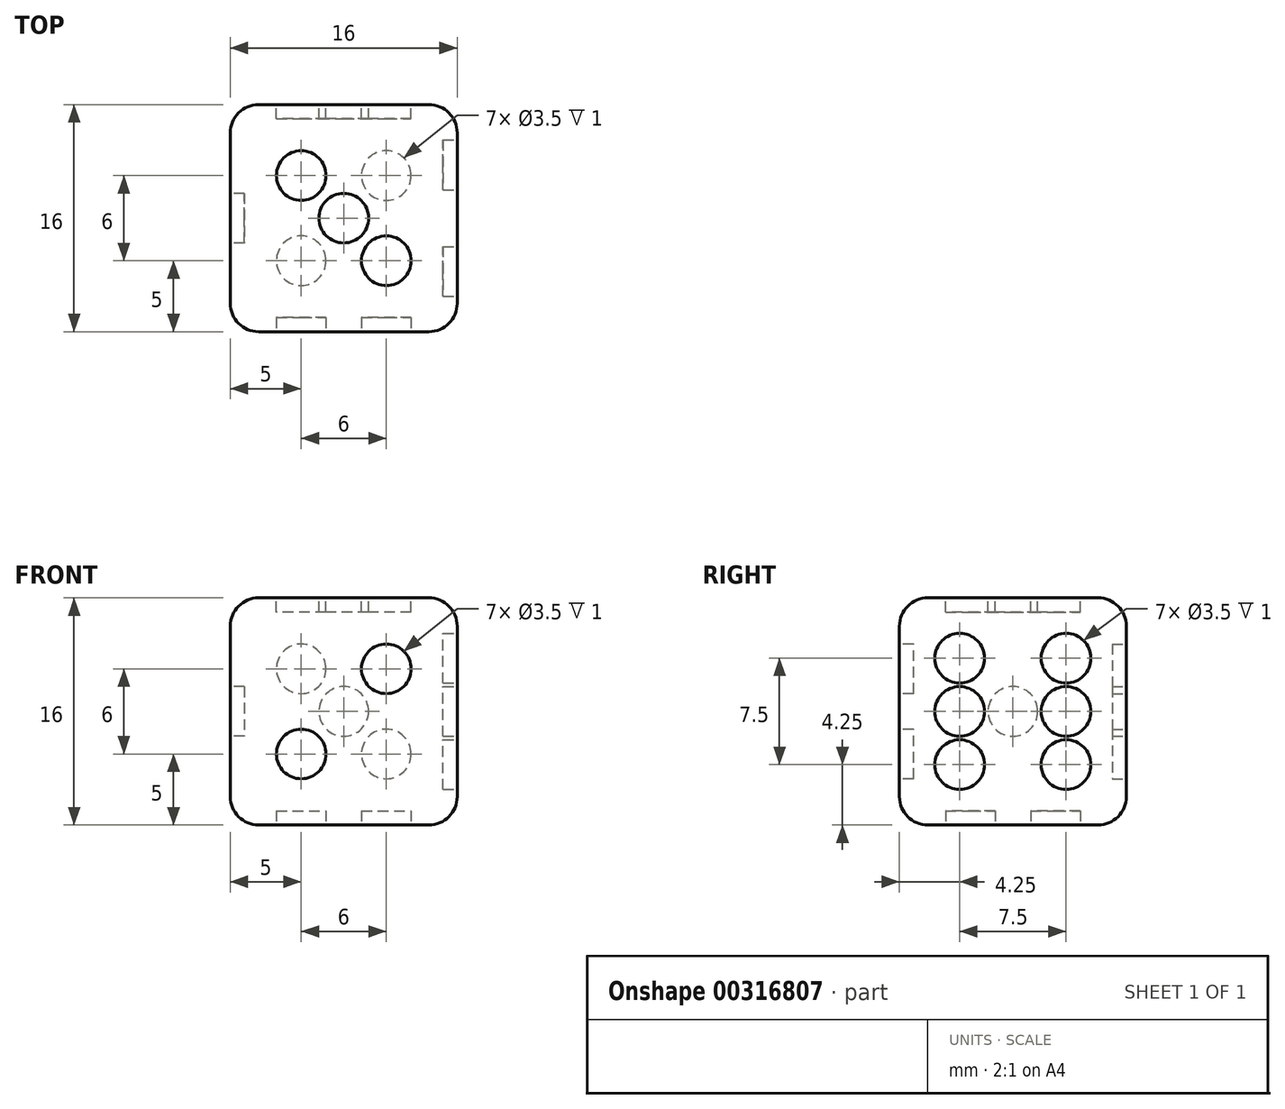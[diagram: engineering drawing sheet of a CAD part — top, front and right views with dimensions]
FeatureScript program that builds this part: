
annotation { "Feature Type Name" : "Feature", "Feature Type Description" : "" }
export const myFeature = defineFeature(function(context is Context, id is Id, definition is map)
    precondition{}
    {
        {
            var Q0;
            Q0=qCreatedBy(makeId("Front.planeOp"),FACE);
            var sketch = newSketch(context, id + "F0", { "sketchPlane" : qUnion([Q0])});
            skLineSegment(sketch, "E0.bottom", {"start": v(8, 8) * mm, "end": v(-8, 8) * mm});
            skLineSegment(sketch, "E0.top", {"start": v(8, -8) * mm, "end": v(-8, -8) * mm});
            skLineSegment(sketch, "E0.left", {"start": v(8, 8) * mm, "end": v(8, -8) * mm});
            skLineSegment(sketch, "E0.right", {"start": v(-8, 8) * mm, "end": v(-8, -8) * mm});
            skPoint(sketch, "E0.middle", {"position": v(0, 0) * mm});
            skSolve(sketch);
        }
        {
            var Q0;
            Q0 = qSketchRegion(id + "F0", true);
            extrude(context, id + "F1", {"entities" : qUnion([Q0]), "depth" : 16 * mm});
        }
        {
            var Q0;
            Q0=makeQuery(id+"F1.opExtrude","CAP_EDGE",EDGE,{"disambiguationData":[OSD([sQuery(id+"F0.wireOp",EDGE,"E0.bottom")])],"isStart":false});
            var Q1;
            Q1=makeQuery(id+"F1.opExtrude","SWEPT_EDGE",EDGE,{"disambiguationData":[OSD([sQuery(id+"F0.wireOp",EDGE,"E0.bottom"),sQuery(id+"F0.wireOp",EDGE,"E0.right")])]});
            var Q2;
            Q2=makeQuery(id+"F1.opExtrude","SWEPT_EDGE",EDGE,{"disambiguationData":[OSD([sQuery(id+"F0.wireOp",EDGE,"E0.bottom"),sQuery(id+"F0.wireOp",EDGE,"E0.left")])]});
            var Q3;
            Q3=makeQuery(id+"F1.opExtrude","CAP_EDGE",EDGE,{"disambiguationData":[OSD([sQuery(id+"F0.wireOp",EDGE,"E0.bottom")])],"isStart":true});
            var Q4;
            Q4=makeQuery(id+"F1.opExtrude","CAP_EDGE",EDGE,{"disambiguationData":[OSD([sQuery(id+"F0.wireOp",EDGE,"E0.top")])],"isStart":true});
            var Q5;
            Q5=makeQuery(id+"F1.opExtrude","CAP_EDGE",EDGE,{"disambiguationData":[OSD([sQuery(id+"F0.wireOp",EDGE,"E0.left")])],"isStart":true});
            var Q6;
            Q6=makeQuery(id+"F1.opExtrude","SWEPT_EDGE",EDGE,{"disambiguationData":[OSD([sQuery(id+"F0.wireOp",EDGE,"E0.top"),sQuery(id+"F0.wireOp",EDGE,"E0.right")])]});
            var Q7;
            Q7=makeQuery(id+"F1.opExtrude","CAP_EDGE",EDGE,{"disambiguationData":[OSD([sQuery(id+"F0.wireOp",EDGE,"E0.right")])],"isStart":false});
            var Q8;
            Q8=makeQuery(id+"F1.opExtrude","CAP_EDGE",EDGE,{"disambiguationData":[OSD([sQuery(id+"F0.wireOp",EDGE,"E0.right")])],"isStart":true});
            var Q9;
            Q9=makeQuery(id+"F1.opExtrude","CAP_EDGE",EDGE,{"disambiguationData":[OSD([sQuery(id+"F0.wireOp",EDGE,"E0.top")])],"isStart":false});
            var Q10;
            Q10=makeQuery(id+"F1.opExtrude","CAP_EDGE",EDGE,{"disambiguationData":[OSD([sQuery(id+"F0.wireOp",EDGE,"E0.left")])],"isStart":false});
            var Q11;
            Q11=makeQuery(id+"F1.opExtrude","SWEPT_EDGE",EDGE,{"disambiguationData":[OSD([sQuery(id+"F0.wireOp",EDGE,"E0.top"),sQuery(id+"F0.wireOp",EDGE,"E0.left")])]});
            fillet(context, id + "F2", {"entities" : qUnion([Q0, Q1, Q2, Q3, Q4, Q5, Q6, Q7, Q8, Q9, Q10, Q11]), "radius" : 2 * mm, "tangentPropagation" : true, "allowEdgeOverflow" : false});
        }
        {
            var Q0;
            Q0=makeQuery(id+"F1.opExtrude","CAP_FACE",FACE,{"disambiguationData":[OSD([sQuery(id+"F0.wireOp",EDGE,"E0.bottom"),sQuery(id+"F0.wireOp",EDGE,"E0.top"),sQuery(id+"F0.wireOp",EDGE,"E0.left"),sQuery(id+"F0.wireOp",EDGE,"E0.right")])],"isStart":false});
            var sketch = newSketch(context, id + "F3", { "sketchPlane" : qUnion([Q0])});
            skLineSegment(sketch, "E1.bottom", {"start": v(3, 3) * mm, "end": v(-3, 3) * mm});
            skLineSegment(sketch, "E1.top", {"start": v(3, -3) * mm, "end": v(-3, -3) * mm});
            skLineSegment(sketch, "E1.left", {"start": v(3, 3) * mm, "end": v(3, -3) * mm});
            skLineSegment(sketch, "E1.right", {"start": v(-3, 3) * mm, "end": v(-3, -3) * mm});
            skPoint(sketch, "E1.middle", {"position": v(0, 0) * mm});
            skCircle(sketch, "E2", {"center": v(-3, -3) * mm, "radius": 1.75 * mm});
            skCircle(sketch, "E3", {"center": v(3, 3) * mm, "radius": 1.75 * mm});
            skSolve(sketch);
        }
        {
            var Q0;
            {var subQ0=sQuery(id+"F3.wireOp",EDGE,"E1.left");var subQ1=sQuery(id+"F3.wireOp",EDGE,"E1.bottom");var subQ2=makeQuery(id+"F3.imprint","INTERSECT",VERTEX,{"derivedFrom":[subQ1,subQ0]});Q0=makeQuery(id+"F3.imprint","IMPRINT",FACE,{"disambiguationData":[TD([[makeQuery(id+"F3.imprint","IMPRINT",EDGE,{"disambiguationData":[TD([[subQ2,-1.0]])],"derivedFrom":subQ1}),1.0]])]});}
            var Q1;
            {var subQ0=sQuery(id+"F3.wireOp",EDGE,"E1.right");var subQ1=sQuery(id+"F3.wireOp",EDGE,"E1.top");var subQ2=makeQuery(id+"F3.imprint","INTERSECT",VERTEX,{"derivedFrom":[subQ1,subQ0]});Q1=makeQuery(id+"F3.imprint","IMPRINT",FACE,{"disambiguationData":[TD([[makeQuery(id+"F3.imprint","IMPRINT",EDGE,{"disambiguationData":[TD([[subQ2,1.0]])],"derivedFrom":subQ1}),1.0]])]});}
            var Q2;
            {var subQ0=sQuery(id+"F3.wireOp",EDGE,"E1.right");var subQ1=sQuery(id+"F3.wireOp",EDGE,"E1.top");var subQ2=makeQuery(id+"F3.imprint","INTERSECT",VERTEX,{"derivedFrom":[subQ1,subQ0]});Q2=makeQuery(id+"F3.imprint","IMPRINT",FACE,{"disambiguationData":[TD([[makeQuery(id+"F3.imprint","IMPRINT",EDGE,{"disambiguationData":[TD([[subQ2,1.0]])],"derivedFrom":subQ1}),-1.0]])]});}
            var Q3;
            {var subQ0=sQuery(id+"F3.wireOp",EDGE,"E1.left");var subQ1=sQuery(id+"F3.wireOp",EDGE,"E1.bottom");var subQ2=makeQuery(id+"F3.imprint","INTERSECT",VERTEX,{"derivedFrom":[subQ1,subQ0]});Q3=makeQuery(id+"F3.imprint","IMPRINT",FACE,{"disambiguationData":[TD([[makeQuery(id+"F3.imprint","IMPRINT",EDGE,{"disambiguationData":[TD([[subQ2,-1.0]])],"derivedFrom":subQ1}),-1.0]])]});}
            extrude(context, id + "F4", {"entities" : qUnion([Q0, Q1, Q2, Q3]), "operationType" : NewBodyOperationType.REMOVE, "oppositeDirection" : true, "depth" : 1 * mm});
        }
        {
            var Q0;
            Q0=makeQuery(id+"F1.opExtrude","SWEPT_FACE",FACE,{"disambiguationData":[OSD([sQuery(id+"F0.wireOp",EDGE,"E0.bottom")])]});
            var sketch = newSketch(context, id + "F5", { "sketchPlane" : qUnion([Q0])});
            skLineSegment(sketch, "E4.bottom", {"start": v(3, -5) * mm, "end": v(-3, -5) * mm});
            skLineSegment(sketch, "E4.top", {"start": v(3, -11) * mm, "end": v(-3, -11) * mm});
            skLineSegment(sketch, "E4.left", {"start": v(3, -5) * mm, "end": v(3, -11) * mm});
            skLineSegment(sketch, "E4.right", {"start": v(-3, -5) * mm, "end": v(-3, -11) * mm});
            skPoint(sketch, "E4.middle", {"position": v(0, -8) * mm});
            skPoint(sketch, "E4.middle.positionSnap0", {"position": v(6, -8) * mm});
            skPoint(sketch, "E4.middle.positionSnap1", {"position": v(0, -14) * mm});
            skPoint(sketch, "E4.centerSnap0", {"position": v(6, -8) * mm});
            skPoint(sketch, "E4.centerSnap1", {"position": v(0, -14) * mm});
            skCircle(sketch, "E5", {"center": v(3, -11) * mm, "radius": 1.75 * mm});
            skCircle(sketch, "E6", {"center": v(0, -8) * mm, "radius": 1.75 * mm});
            skCircle(sketch, "E7", {"center": v(-3, -5) * mm, "radius": 1.75 * mm});
            skSolve(sketch);
        }
        {
            var Q0;
            {var subQ0=sQuery(id+"F5.wireOp",EDGE,"E4.right");var subQ1=sQuery(id+"F5.wireOp",EDGE,"E4.bottom");var subQ2=makeQuery(id+"F5.imprint","INTERSECT",VERTEX,{"derivedFrom":[subQ1,subQ0]});Q0=makeQuery(id+"F5.imprint","IMPRINT",FACE,{"disambiguationData":[TD([[makeQuery(id+"F5.imprint","IMPRINT",EDGE,{"disambiguationData":[TD([[subQ2,1.0]])],"derivedFrom":subQ1}),-1.0]])]});}
            var Q1;
            {var subQ0=sQuery(id+"F5.wireOp",EDGE,"E4.right");var subQ1=sQuery(id+"F5.wireOp",EDGE,"E4.bottom");var subQ2=makeQuery(id+"F5.imprint","INTERSECT",VERTEX,{"derivedFrom":[subQ1,subQ0]});Q1=makeQuery(id+"F5.imprint","IMPRINT",FACE,{"disambiguationData":[TD([[makeQuery(id+"F5.imprint","IMPRINT",EDGE,{"disambiguationData":[TD([[subQ2,1.0]])],"derivedFrom":subQ1}),1.0]])]});}
            var Q2;
            {var subQ0=sQuery(id+"F5.wireOp",EDGE,"E4.left");var subQ1=sQuery(id+"F5.wireOp",EDGE,"E4.top");var subQ2=makeQuery(id+"F5.imprint","INTERSECT",VERTEX,{"derivedFrom":[subQ1,subQ0]});Q2=makeQuery(id+"F5.imprint","IMPRINT",FACE,{"disambiguationData":[TD([[makeQuery(id+"F5.imprint","IMPRINT",EDGE,{"disambiguationData":[TD([[subQ2,-1.0]])],"derivedFrom":subQ1}),-1.0]])]});}
            var Q3;
            {var subQ0=sQuery(id+"F5.wireOp",EDGE,"E4.left");var subQ1=sQuery(id+"F5.wireOp",EDGE,"E4.top");var subQ2=makeQuery(id+"F5.imprint","INTERSECT",VERTEX,{"derivedFrom":[subQ1,subQ0]});Q3=makeQuery(id+"F5.imprint","IMPRINT",FACE,{"disambiguationData":[TD([[makeQuery(id+"F5.imprint","IMPRINT",EDGE,{"disambiguationData":[TD([[subQ2,-1.0]])],"derivedFrom":subQ1}),1.0]])]});}
            var Q4;
            Q4=makeQuery(id+"F5.imprint","IMPRINT",FACE,{"disambiguationData":[TD([[makeQuery(id+"F5.imprint","IMPRINT",EDGE,{"derivedFrom":sQuery(id+"F5.wireOp",EDGE,"E6")}),1.0]])]});
            extrude(context, id + "F6", {"entities" : qUnion([Q0, Q1, Q2, Q3, Q4]), "operationType" : NewBodyOperationType.REMOVE, "oppositeDirection" : true, "depth" : 1 * mm});
        }
        {
            var Q0;
            Q0=makeQuery(id+"F1.opExtrude","SWEPT_FACE",FACE,{"disambiguationData":[OSD([sQuery(id+"F0.wireOp",EDGE,"E0.left")])]});
            var sketch = newSketch(context, id + "F7", { "sketchPlane" : qUnion([Q0])});
            skLineSegment(sketch, "E8.bottom", {"start": v(-4.25, 3.75) * mm, "end": v(-11.75, 3.75) * mm});
            skLineSegment(sketch, "E8.top", {"start": v(-4.25, -3.75) * mm, "end": v(-11.75, -3.75) * mm});
            skLineSegment(sketch, "E8.left", {"start": v(-4.25, 3.75) * mm, "end": v(-4.25, -3.75) * mm});
            skLineSegment(sketch, "E8.right", {"start": v(-11.75, 3.75) * mm, "end": v(-11.75, -3.75) * mm});
            skPoint(sketch, "E8.middle", {"position": v(-8, 0) * mm});
            skPoint(sketch, "E8.middle.positionSnap0", {"position": v(-8, -6) * mm});
            skPoint(sketch, "E8.middle.positionSnap1", {"position": v(-14, 0) * mm});
            skPoint(sketch, "E8.centerSnap0", {"position": v(-8, -6) * mm});
            skPoint(sketch, "E8.centerSnap1", {"position": v(-14, 0) * mm});
            skCircle(sketch, "E9", {"center": v(-11.75, 3.75) * mm, "radius": 1.75 * mm});
            skCircle(sketch, "E10", {"center": v(-4.25, 3.75) * mm, "radius": 1.75 * mm});
            skCircle(sketch, "E11", {"center": v(-4.25, 0) * mm, "radius": 1.75 * mm});
            skCircle(sketch, "E12", {"center": v(-4.25, -3.75) * mm, "radius": 1.75 * mm});
            skCircle(sketch, "E13", {"center": v(-11.75, -3.75) * mm, "radius": 1.75 * mm});
            skCircle(sketch, "E14", {"center": v(-11.75, 0) * mm, "radius": 1.75 * mm});
            skSolve(sketch);
        }
        {
            var Q0;
            {var subQ0=sQuery(id+"F7.wireOp",EDGE,"E8.left");var subQ1=sQuery(id+"F7.wireOp",EDGE,"E8.bottom");var subQ2=makeQuery(id+"F7.imprint","INTERSECT",VERTEX,{"derivedFrom":[subQ1,subQ0]});Q0=makeQuery(id+"F7.imprint","IMPRINT",FACE,{"disambiguationData":[TD([[makeQuery(id+"F7.imprint","IMPRINT",EDGE,{"disambiguationData":[TD([[subQ2,-1.0]])],"derivedFrom":subQ1}),1.0]])]});}
            var Q1;
            {var subQ0=sQuery(id+"F7.wireOp",EDGE,"E8.left");var subQ1=sQuery(id+"F7.wireOp",EDGE,"E8.bottom");var subQ2=makeQuery(id+"F7.imprint","INTERSECT",VERTEX,{"derivedFrom":[subQ1,subQ0]});Q1=makeQuery(id+"F7.imprint","IMPRINT",FACE,{"disambiguationData":[TD([[makeQuery(id+"F7.imprint","IMPRINT",EDGE,{"disambiguationData":[TD([[subQ2,-1.0]])],"derivedFrom":subQ1}),-1.0]])]});}
            var Q2;
            {var subQ0=sQuery(id+"F7.wireOp",EDGE,"E8.right");var subQ1=sQuery(id+"F7.wireOp",EDGE,"E8.bottom");var subQ2=makeQuery(id+"F7.imprint","INTERSECT",VERTEX,{"derivedFrom":[subQ1,subQ0]});Q2=makeQuery(id+"F7.imprint","IMPRINT",FACE,{"disambiguationData":[TD([[makeQuery(id+"F7.imprint","IMPRINT",EDGE,{"disambiguationData":[TD([[subQ2,1.0]])],"derivedFrom":subQ1}),-1.0]])]});}
            var Q3;
            {var subQ0=sQuery(id+"F7.wireOp",EDGE,"E8.right");var subQ1=sQuery(id+"F7.wireOp",EDGE,"E8.bottom");var subQ2=makeQuery(id+"F7.imprint","INTERSECT",VERTEX,{"derivedFrom":[subQ1,subQ0]});Q3=makeQuery(id+"F7.imprint","IMPRINT",FACE,{"disambiguationData":[TD([[makeQuery(id+"F7.imprint","IMPRINT",EDGE,{"disambiguationData":[TD([[subQ2,1.0]])],"derivedFrom":subQ1}),1.0]])]});}
            var Q4;
            {var subQ0=sQuery(id+"F7.wireOp",EDGE,"E8.left");var subQ1=sQuery(id+"F7.wireOp",EDGE,"E8.top");var subQ2=makeQuery(id+"F7.imprint","INTERSECT",VERTEX,{"derivedFrom":[subQ1,subQ0]});Q4=makeQuery(id+"F7.imprint","IMPRINT",FACE,{"disambiguationData":[TD([[makeQuery(id+"F7.imprint","IMPRINT",EDGE,{"disambiguationData":[TD([[subQ2,-1.0]])],"derivedFrom":subQ1}),-1.0]])]});}
            var Q5;
            {var subQ0=sQuery(id+"F7.wireOp",EDGE,"E8.left");var subQ1=sQuery(id+"F7.wireOp",EDGE,"E8.top");var subQ2=makeQuery(id+"F7.imprint","INTERSECT",VERTEX,{"derivedFrom":[subQ1,subQ0]});Q5=makeQuery(id+"F7.imprint","IMPRINT",FACE,{"disambiguationData":[TD([[makeQuery(id+"F7.imprint","IMPRINT",EDGE,{"disambiguationData":[TD([[subQ2,-1.0]])],"derivedFrom":subQ1}),1.0]])]});}
            var Q6;
            {var subQ0=sQuery(id+"F7.wireOp",EDGE,"E8.right");var subQ1=sQuery(id+"F7.wireOp",EDGE,"E8.top");var subQ2=makeQuery(id+"F7.imprint","INTERSECT",VERTEX,{"derivedFrom":[subQ1,subQ0]});Q6=makeQuery(id+"F7.imprint","IMPRINT",FACE,{"disambiguationData":[TD([[makeQuery(id+"F7.imprint","IMPRINT",EDGE,{"disambiguationData":[TD([[subQ2,1.0]])],"derivedFrom":subQ1}),-1.0]])]});}
            var Q7;
            {var subQ0=sQuery(id+"F7.wireOp",EDGE,"E8.right");var subQ1=sQuery(id+"F7.wireOp",EDGE,"E8.top");var subQ2=makeQuery(id+"F7.imprint","INTERSECT",VERTEX,{"derivedFrom":[subQ1,subQ0]});Q7=makeQuery(id+"F7.imprint","IMPRINT",FACE,{"disambiguationData":[TD([[makeQuery(id+"F7.imprint","IMPRINT",EDGE,{"disambiguationData":[TD([[subQ2,1.0]])],"derivedFrom":subQ1}),1.0]])]});}
            var Q8;
            {var subQ0=sQuery(id+"F7.wireOp",EDGE,"E11");var subQ1=sQuery(id+"F7.wireOp",EDGE,"E8.left");var subQ2=makeQuery(id+"F7.imprint","INTERSECT",VERTEX,{"disambiguationData":[OD(0.0)],"derivedFrom":[subQ1,subQ0]});Q8=makeQuery(id+"F7.imprint","IMPRINT",FACE,{"disambiguationData":[TD([[makeQuery(id+"F7.imprint","IMPRINT",EDGE,{"disambiguationData":[TD([[subQ2,-1.0]])],"derivedFrom":subQ1}),-1.0]])]});}
            var Q9;
            {var subQ0=sQuery(id+"F7.wireOp",EDGE,"E11");var subQ1=sQuery(id+"F7.wireOp",EDGE,"E8.left");var subQ2=makeQuery(id+"F7.imprint","INTERSECT",VERTEX,{"disambiguationData":[OD(0.0)],"derivedFrom":[subQ1,subQ0]});Q9=makeQuery(id+"F7.imprint","IMPRINT",FACE,{"disambiguationData":[TD([[makeQuery(id+"F7.imprint","IMPRINT",EDGE,{"disambiguationData":[TD([[subQ2,-1.0]])],"derivedFrom":subQ1}),1.0]])]});}
            var Q10;
            {var subQ0=sQuery(id+"F7.wireOp",EDGE,"E14");var subQ1=sQuery(id+"F7.wireOp",EDGE,"E8.right");var subQ2=makeQuery(id+"F7.imprint","INTERSECT",VERTEX,{"disambiguationData":[OD(0.0)],"derivedFrom":[subQ1,subQ0]});Q10=makeQuery(id+"F7.imprint","IMPRINT",FACE,{"disambiguationData":[TD([[makeQuery(id+"F7.imprint","IMPRINT",EDGE,{"disambiguationData":[TD([[subQ2,-1.0]])],"derivedFrom":subQ1}),-1.0]])]});}
            var Q11;
            {var subQ0=sQuery(id+"F7.wireOp",EDGE,"E14");var subQ1=sQuery(id+"F7.wireOp",EDGE,"E8.right");var subQ2=makeQuery(id+"F7.imprint","INTERSECT",VERTEX,{"disambiguationData":[OD(0.0)],"derivedFrom":[subQ1,subQ0]});Q11=makeQuery(id+"F7.imprint","IMPRINT",FACE,{"disambiguationData":[TD([[makeQuery(id+"F7.imprint","IMPRINT",EDGE,{"disambiguationData":[TD([[subQ2,-1.0]])],"derivedFrom":subQ1}),1.0]])]});}
            extrude(context, id + "F8", {"entities" : qUnion([Q0, Q1, Q2, Q3, Q4, Q5, Q6, Q7, Q8, Q9, Q10, Q11]), "operationType" : NewBodyOperationType.REMOVE, "oppositeDirection" : true, "depth" : 1 * mm});
        }
        {
            var Q0;
            Q0=makeQuery(id+"F1.opExtrude","SWEPT_FACE",FACE,{"disambiguationData":[OSD([sQuery(id+"F0.wireOp",EDGE,"E0.top")])]});
            var sketch = newSketch(context, id + "F9", { "sketchPlane" : qUnion([Q0])});
            skLineSegment(sketch, "E15.bottom", {"start": v(3, 11) * mm, "end": v(-3, 11) * mm});
            skLineSegment(sketch, "E15.top", {"start": v(3, 5) * mm, "end": v(-3, 5) * mm});
            skLineSegment(sketch, "E15.left", {"start": v(3, 11) * mm, "end": v(3, 5) * mm});
            skLineSegment(sketch, "E15.right", {"start": v(-3, 11) * mm, "end": v(-3, 5) * mm});
            skPoint(sketch, "E15.middle", {"position": v(0, 8) * mm});
            skPoint(sketch, "E15.middle.positionSnap0", {"position": v(6, 8) * mm});
            skPoint(sketch, "E15.centerSnap0", {"position": v(6, 8) * mm});
            skCircle(sketch, "E16", {"center": v(-3, 11) * mm, "radius": 1.75 * mm});
            skCircle(sketch, "E17", {"center": v(3, 11) * mm, "radius": 1.75 * mm});
            skCircle(sketch, "E18", {"center": v(3, 5) * mm, "radius": 1.75 * mm});
            skCircle(sketch, "E19", {"center": v(-3, 5) * mm, "radius": 1.75 * mm});
            skSolve(sketch);
        }
        {
            var Q0;
            {var subQ0=sQuery(id+"F9.wireOp",EDGE,"E15.left");var subQ1=sQuery(id+"F9.wireOp",EDGE,"E15.bottom");var subQ2=makeQuery(id+"F9.imprint","INTERSECT",VERTEX,{"derivedFrom":[subQ1,subQ0]});Q0=makeQuery(id+"F9.imprint","IMPRINT",FACE,{"disambiguationData":[TD([[makeQuery(id+"F9.imprint","IMPRINT",EDGE,{"disambiguationData":[TD([[subQ2,-1.0]])],"derivedFrom":subQ1}),1.0]])]});}
            var Q1;
            {var subQ0=sQuery(id+"F9.wireOp",EDGE,"E15.left");var subQ1=sQuery(id+"F9.wireOp",EDGE,"E15.bottom");var subQ2=makeQuery(id+"F9.imprint","INTERSECT",VERTEX,{"derivedFrom":[subQ1,subQ0]});Q1=makeQuery(id+"F9.imprint","IMPRINT",FACE,{"disambiguationData":[TD([[makeQuery(id+"F9.imprint","IMPRINT",EDGE,{"disambiguationData":[TD([[subQ2,-1.0]])],"derivedFrom":subQ1}),-1.0]])]});}
            var Q2;
            {var subQ0=sQuery(id+"F9.wireOp",EDGE,"E15.right");var subQ1=sQuery(id+"F9.wireOp",EDGE,"E15.bottom");var subQ2=makeQuery(id+"F9.imprint","INTERSECT",VERTEX,{"derivedFrom":[subQ1,subQ0]});Q2=makeQuery(id+"F9.imprint","IMPRINT",FACE,{"disambiguationData":[TD([[makeQuery(id+"F9.imprint","IMPRINT",EDGE,{"disambiguationData":[TD([[subQ2,1.0]])],"derivedFrom":subQ1}),-1.0]])]});}
            var Q3;
            {var subQ0=sQuery(id+"F9.wireOp",EDGE,"E15.right");var subQ1=sQuery(id+"F9.wireOp",EDGE,"E15.bottom");var subQ2=makeQuery(id+"F9.imprint","INTERSECT",VERTEX,{"derivedFrom":[subQ1,subQ0]});Q3=makeQuery(id+"F9.imprint","IMPRINT",FACE,{"disambiguationData":[TD([[makeQuery(id+"F9.imprint","IMPRINT",EDGE,{"disambiguationData":[TD([[subQ2,1.0]])],"derivedFrom":subQ1}),1.0]])]});}
            var Q4;
            {var subQ0=sQuery(id+"F9.wireOp",EDGE,"E15.left");var subQ1=sQuery(id+"F9.wireOp",EDGE,"E15.top");var subQ2=makeQuery(id+"F9.imprint","INTERSECT",VERTEX,{"derivedFrom":[subQ1,subQ0]});Q4=makeQuery(id+"F9.imprint","IMPRINT",FACE,{"disambiguationData":[TD([[makeQuery(id+"F9.imprint","IMPRINT",EDGE,{"disambiguationData":[TD([[subQ2,-1.0]])],"derivedFrom":subQ1}),-1.0]])]});}
            var Q5;
            {var subQ0=sQuery(id+"F9.wireOp",EDGE,"E15.left");var subQ1=sQuery(id+"F9.wireOp",EDGE,"E15.top");var subQ2=makeQuery(id+"F9.imprint","INTERSECT",VERTEX,{"derivedFrom":[subQ1,subQ0]});Q5=makeQuery(id+"F9.imprint","IMPRINT",FACE,{"disambiguationData":[TD([[makeQuery(id+"F9.imprint","IMPRINT",EDGE,{"disambiguationData":[TD([[subQ2,-1.0]])],"derivedFrom":subQ1}),1.0]])]});}
            var Q6;
            {var subQ0=sQuery(id+"F9.wireOp",EDGE,"E15.right");var subQ1=sQuery(id+"F9.wireOp",EDGE,"E15.top");var subQ2=makeQuery(id+"F9.imprint","INTERSECT",VERTEX,{"derivedFrom":[subQ1,subQ0]});Q6=makeQuery(id+"F9.imprint","IMPRINT",FACE,{"disambiguationData":[TD([[makeQuery(id+"F9.imprint","IMPRINT",EDGE,{"disambiguationData":[TD([[subQ2,1.0]])],"derivedFrom":subQ1}),-1.0]])]});}
            var Q7;
            {var subQ0=sQuery(id+"F9.wireOp",EDGE,"E15.right");var subQ1=sQuery(id+"F9.wireOp",EDGE,"E15.top");var subQ2=makeQuery(id+"F9.imprint","INTERSECT",VERTEX,{"derivedFrom":[subQ1,subQ0]});Q7=makeQuery(id+"F9.imprint","IMPRINT",FACE,{"disambiguationData":[TD([[makeQuery(id+"F9.imprint","IMPRINT",EDGE,{"disambiguationData":[TD([[subQ2,1.0]])],"derivedFrom":subQ1}),1.0]])]});}
            extrude(context, id + "F10", {"entities" : qUnion([Q0, Q1, Q2, Q3, Q4, Q5, Q6, Q7]), "operationType" : NewBodyOperationType.REMOVE, "oppositeDirection" : true, "depth" : 1 * mm});
        }
        {
            var Q0;
            Q0=makeQuery(id+"F1.opExtrude","SWEPT_FACE",FACE,{"disambiguationData":[OSD([sQuery(id+"F0.wireOp",EDGE,"E0.right")])]});
            var sketch = newSketch(context, id + "F11", { "sketchPlane" : qUnion([Q0])});
            skCircle(sketch, "E20", {"center": v(8, 0) * mm, "radius": 1.75 * mm});
            skPoint(sketch, "E20.centerSnap0", {"position": v(8, -6) * mm});
            skSolve(sketch);
        }
        {
            var Q0;
            Q0 = qSketchRegion(id + "F11", true);
            extrude(context, id + "F12", {"entities" : qUnion([Q0]), "operationType" : NewBodyOperationType.REMOVE, "oppositeDirection" : true, "depth" : 1 * mm});
        }
        {
            var Q0;
            Q0=makeQuery(id+"F1.opExtrude","CAP_FACE",FACE,{"disambiguationData":[OSD([sQuery(id+"F0.wireOp",EDGE,"E0.bottom"),sQuery(id+"F0.wireOp",EDGE,"E0.top"),sQuery(id+"F0.wireOp",EDGE,"E0.left"),sQuery(id+"F0.wireOp",EDGE,"E0.right")])],"isStart":true});
            var sketch = newSketch(context, id + "F13", { "sketchPlane" : qUnion([Q0])});
            skLineSegment(sketch, "E21.bottom", {"start": v(3, 3) * mm, "end": v(-3, 3) * mm});
            skLineSegment(sketch, "E21.top", {"start": v(3, -3) * mm, "end": v(-3, -3) * mm});
            skLineSegment(sketch, "E21.left", {"start": v(3, 3) * mm, "end": v(3, -3) * mm});
            skLineSegment(sketch, "E21.right", {"start": v(-3, 3) * mm, "end": v(-3, -3) * mm});
            skPoint(sketch, "E21.middle", {"position": v(0, 0) * mm});
            skCircle(sketch, "E22", {"center": v(-3, 3) * mm, "radius": 1.75 * mm});
            skCircle(sketch, "E23", {"center": v(-3, -3) * mm, "radius": 1.75 * mm});
            skCircle(sketch, "E24", {"center": v(0, 0) * mm, "radius": 1.75 * mm});
            skCircle(sketch, "E25", {"center": v(3, 3) * mm, "radius": 1.75 * mm});
            skCircle(sketch, "E26", {"center": v(3, -3) * mm, "radius": 1.75 * mm});
            skSolve(sketch);
        }
        {
            var Q0;
            {var subQ0=sQuery(id+"F13.wireOp",EDGE,"E21.left");var subQ1=sQuery(id+"F13.wireOp",EDGE,"E21.bottom");var subQ2=makeQuery(id+"F13.imprint","INTERSECT",VERTEX,{"derivedFrom":[subQ1,subQ0]});Q0=makeQuery(id+"F13.imprint","IMPRINT",FACE,{"disambiguationData":[TD([[makeQuery(id+"F13.imprint","IMPRINT",EDGE,{"disambiguationData":[TD([[subQ2,-1.0]])],"derivedFrom":subQ1}),1.0]])]});}
            var Q1;
            {var subQ0=sQuery(id+"F13.wireOp",EDGE,"E21.left");var subQ1=sQuery(id+"F13.wireOp",EDGE,"E21.bottom");var subQ2=makeQuery(id+"F13.imprint","INTERSECT",VERTEX,{"derivedFrom":[subQ1,subQ0]});Q1=makeQuery(id+"F13.imprint","IMPRINT",FACE,{"disambiguationData":[TD([[makeQuery(id+"F13.imprint","IMPRINT",EDGE,{"disambiguationData":[TD([[subQ2,-1.0]])],"derivedFrom":subQ1}),-1.0]])]});}
            var Q2;
            {var subQ0=sQuery(id+"F13.wireOp",EDGE,"E21.right");var subQ1=sQuery(id+"F13.wireOp",EDGE,"E21.bottom");var subQ2=makeQuery(id+"F13.imprint","INTERSECT",VERTEX,{"derivedFrom":[subQ1,subQ0]});Q2=makeQuery(id+"F13.imprint","IMPRINT",FACE,{"disambiguationData":[TD([[makeQuery(id+"F13.imprint","IMPRINT",EDGE,{"disambiguationData":[TD([[subQ2,1.0]])],"derivedFrom":subQ1}),-1.0]])]});}
            var Q3;
            {var subQ0=sQuery(id+"F13.wireOp",EDGE,"E21.right");var subQ1=sQuery(id+"F13.wireOp",EDGE,"E21.bottom");var subQ2=makeQuery(id+"F13.imprint","INTERSECT",VERTEX,{"derivedFrom":[subQ1,subQ0]});Q3=makeQuery(id+"F13.imprint","IMPRINT",FACE,{"disambiguationData":[TD([[makeQuery(id+"F13.imprint","IMPRINT",EDGE,{"disambiguationData":[TD([[subQ2,1.0]])],"derivedFrom":subQ1}),1.0]])]});}
            var Q4;
            {var subQ0=sQuery(id+"F13.wireOp",EDGE,"E21.left");var subQ1=sQuery(id+"F13.wireOp",EDGE,"E21.top");var subQ2=makeQuery(id+"F13.imprint","INTERSECT",VERTEX,{"derivedFrom":[subQ1,subQ0]});Q4=makeQuery(id+"F13.imprint","IMPRINT",FACE,{"disambiguationData":[TD([[makeQuery(id+"F13.imprint","IMPRINT",EDGE,{"disambiguationData":[TD([[subQ2,-1.0]])],"derivedFrom":subQ1}),-1.0]])]});}
            var Q5;
            {var subQ0=sQuery(id+"F13.wireOp",EDGE,"E21.left");var subQ1=sQuery(id+"F13.wireOp",EDGE,"E21.top");var subQ2=makeQuery(id+"F13.imprint","INTERSECT",VERTEX,{"derivedFrom":[subQ1,subQ0]});Q5=makeQuery(id+"F13.imprint","IMPRINT",FACE,{"disambiguationData":[TD([[makeQuery(id+"F13.imprint","IMPRINT",EDGE,{"disambiguationData":[TD([[subQ2,-1.0]])],"derivedFrom":subQ1}),1.0]])]});}
            var Q6;
            {var subQ0=sQuery(id+"F13.wireOp",EDGE,"E21.right");var subQ1=sQuery(id+"F13.wireOp",EDGE,"E21.top");var subQ2=makeQuery(id+"F13.imprint","INTERSECT",VERTEX,{"derivedFrom":[subQ1,subQ0]});Q6=makeQuery(id+"F13.imprint","IMPRINT",FACE,{"disambiguationData":[TD([[makeQuery(id+"F13.imprint","IMPRINT",EDGE,{"disambiguationData":[TD([[subQ2,1.0]])],"derivedFrom":subQ1}),-1.0]])]});}
            var Q7;
            {var subQ0=sQuery(id+"F13.wireOp",EDGE,"E21.right");var subQ1=sQuery(id+"F13.wireOp",EDGE,"E21.top");var subQ2=makeQuery(id+"F13.imprint","INTERSECT",VERTEX,{"derivedFrom":[subQ1,subQ0]});Q7=makeQuery(id+"F13.imprint","IMPRINT",FACE,{"disambiguationData":[TD([[makeQuery(id+"F13.imprint","IMPRINT",EDGE,{"disambiguationData":[TD([[subQ2,1.0]])],"derivedFrom":subQ1}),1.0]])]});}
            var Q8;
            Q8=makeQuery(id+"F13.imprint","IMPRINT",FACE,{"disambiguationData":[TD([[makeQuery(id+"F13.imprint","IMPRINT",EDGE,{"derivedFrom":sQuery(id+"F13.wireOp",EDGE,"E24")}),1.0]])]});
            extrude(context, id + "F14", {"entities" : qUnion([Q0, Q1, Q2, Q3, Q4, Q5, Q6, Q7, Q8]), "operationType" : NewBodyOperationType.REMOVE, "oppositeDirection" : true, "depth" : 1 * mm});
        }
    });
